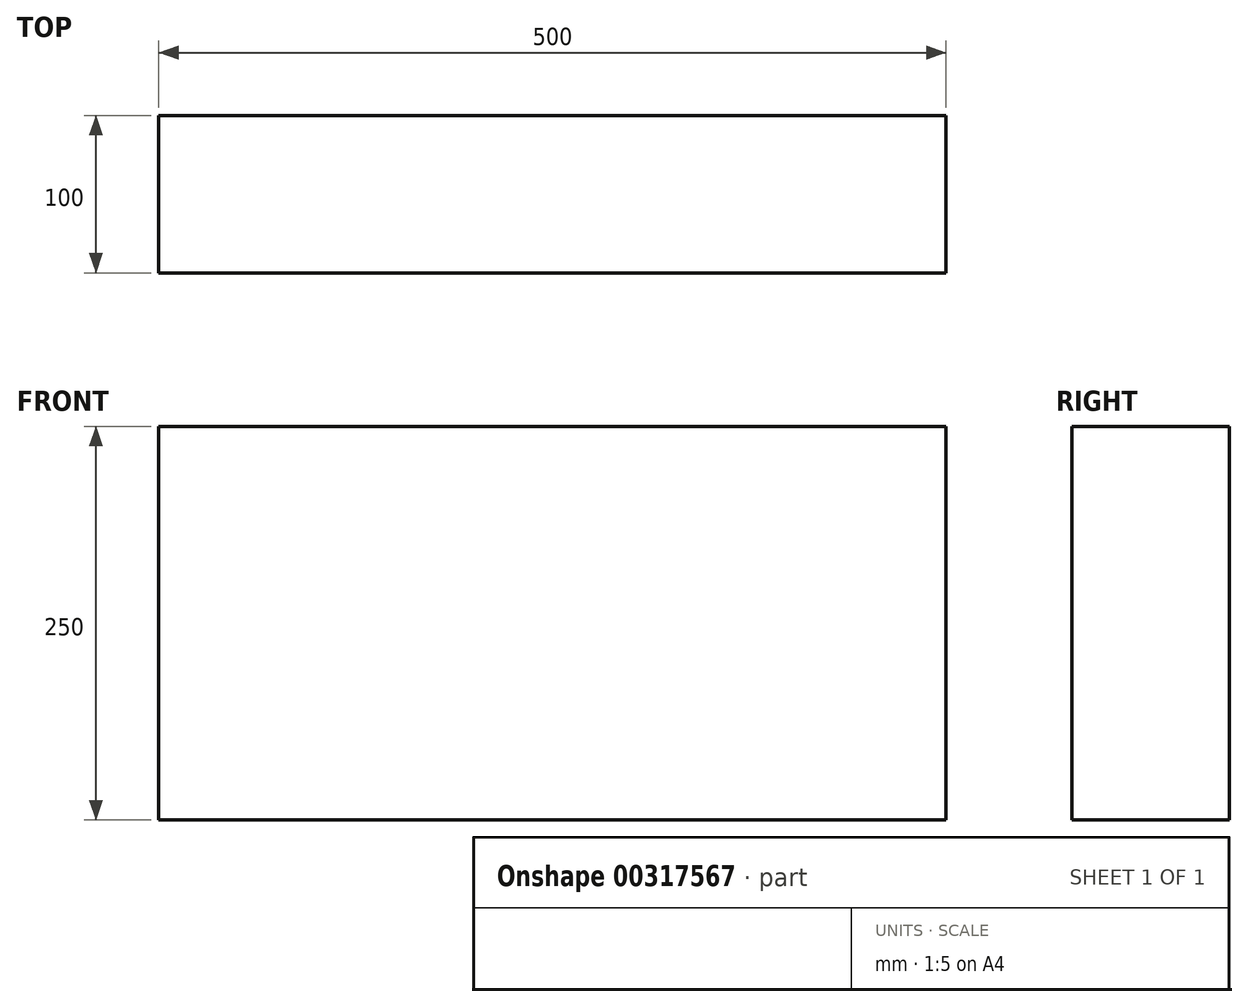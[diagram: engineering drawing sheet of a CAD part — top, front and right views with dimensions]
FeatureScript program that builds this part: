
annotation { "Feature Type Name" : "Feature", "Feature Type Description" : "" }
export const myFeature = defineFeature(function(context is Context, id is Id, definition is map)
    precondition{}
    {
        {
            var Q0;
            Q0=qCreatedBy(makeId("Front.planeOp"),FACE);
            var sketch = newSketch(context, id + "F0", { "sketchPlane" : qUnion([Q0])});
            skLineSegment(sketch, "E0.bottom", {"start": v(0, 250) * mm, "end": v(500, 250) * mm});
            skLineSegment(sketch, "E0.top", {"start": v(0, 0) * mm, "end": v(500, 0) * mm});
            skLineSegment(sketch, "E0.left", {"start": v(0, 250) * mm, "end": v(0, 0) * mm});
            skLineSegment(sketch, "E0.right", {"start": v(500, 250) * mm, "end": v(500, 0) * mm});
            skSolve(sketch);
        }
        {
            var Q0;
            Q0=makeQuery(id+"F0.imprint","IMPRINT",FACE,{"disambiguationData":[TD([[makeQuery(id+"F0.imprint","IMPRINT",EDGE,{"derivedFrom":sQuery(id+"F0.wireOp",EDGE,"E0.bottom")}),-1.0]])]});
            extrude(context, id + "F1", {"entities" : qUnion([Q0]), "depth" : 100 * mm});
        }
    });
